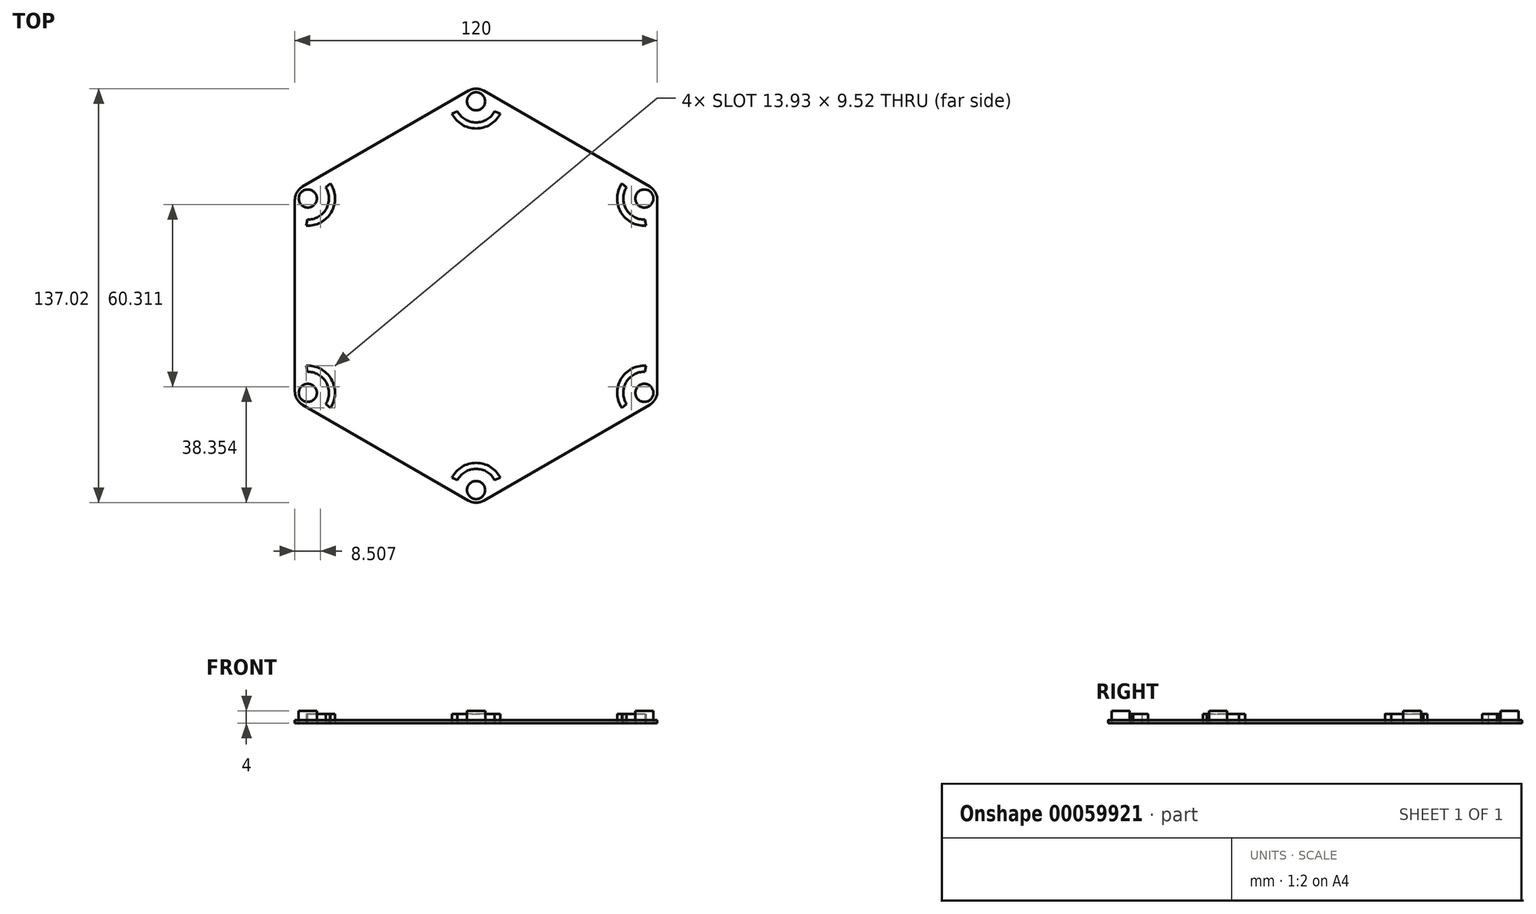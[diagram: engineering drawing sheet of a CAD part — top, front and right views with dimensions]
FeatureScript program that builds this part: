
annotation { "Feature Type Name" : "Feature", "Feature Type Description" : "" }
export const myFeature = defineFeature(function(context is Context, id is Id, definition is map)
    precondition{}
    {
        {
            var Q0;
            Q0=qCreatedBy(makeId("Top.planeOp"),FACE);
            var sketch = newSketch(context, id + "F0", { "sketchPlane" : qUnion([Q0])});
            skCircle(sketch, "E0.cCircle", {"center": v(0, 0) * mm, "radius": 60 * mm, "construction": true});
            skLineSegment(sketch, "E0.0", {"start": v(60, 31.75) * mm, "end": v(60, -31.75) * mm});
            skLineSegment(sketch, "E0.1", {"start": v(57.5, -36.08) * mm, "end": v(2.5, -67.84) * mm});
            skLineSegment(sketch, "E0.2", {"start": v(-2.5, -67.84) * mm, "end": v(-57.5, -36.08) * mm});
            skLineSegment(sketch, "E0.3", {"start": v(-60, -31.75) * mm, "end": v(-60, 31.75) * mm});
            skLineSegment(sketch, "E0.4", {"start": v(-57.5, 36.08) * mm, "end": v(-2.5, 67.84) * mm});
            skLineSegment(sketch, "E0.5", {"start": v(2.5, 67.84) * mm, "end": v(57.5, 36.08) * mm});
            skPoint(sketch, "E0.0.midPoint", {"position": v(60, 0) * mm});
            skCircle(sketch, "E1", {"center": v(0, -64.35) * mm, "radius": 3 * mm});
            skPoint(sketch, "E2.visualSharp", {"position": v(0, -69.28) * mm});
            skArc(sketch, "E2.filletArc", {"start": v(-2.5, -67.84) * mm, "mid": v(0, -68.5) * mm, "end": v(2.5, -67.84) * mm});
            skPoint(sketch, "E3.visualSharp", {"position": v(60, -34.64) * mm});
            skArc(sketch, "E3.filletArc", {"start": v(57.5, -36.08) * mm, "mid": v(59.33, -34.25) * mm, "end": v(60, -31.75) * mm});
            skPoint(sketch, "E4.visualSharp", {"position": v(-60, -34.64) * mm});
            skArc(sketch, "E4.filletArc", {"start": v(-60, -31.75) * mm, "mid": v(-59.33, -34.25) * mm, "end": v(-57.5, -36.08) * mm});
            skPoint(sketch, "E5.visualSharp", {"position": v(60, 34.64) * mm});
            skArc(sketch, "E5.filletArc", {"start": v(60, 31.75) * mm, "mid": v(59.33, 34.25) * mm, "end": v(57.5, 36.08) * mm});
            skPoint(sketch, "E6.visualSharp", {"position": v(-60, 34.64) * mm});
            skArc(sketch, "E6.filletArc", {"start": v(-57.5, 36.08) * mm, "mid": v(-59.33, 34.25) * mm, "end": v(-60, 31.75) * mm});
            skPoint(sketch, "E7.visualSharp", {"position": v(0, 69.28) * mm});
            skArc(sketch, "E7.filletArc", {"start": v(2.5, 67.84) * mm, "mid": v(0, 68.5) * mm, "end": v(-2.5, 67.84) * mm});
            skArc(sketch, "E8.0", {"start": v(6.15, -61.01) * mm, "mid": v(0, -57.35) * mm, "end": v(-6.15, -61.01) * mm});
            skArc(sketch, "E9.0", {"start": v(8.04, -60.31) * mm, "mid": v(0, -55.35) * mm, "end": v(-8.04, -60.31) * mm});
            skLineSegment(sketch, "E10.0", {"start": v(6.15, -61.01) * mm, "end": v(8.04, -60.31) * mm});
            skLineSegment(sketch, "E11.MirrorCS", {"start": v(-6.15, -61.01) * mm, "end": v(-8.04, -60.31) * mm});
            skCircle(sketch, "E12.1.0", {"center": v(-55.73, -32.18) * mm, "radius": 3 * mm});
            skArc(sketch, "E12.1.1", {"start": v(-49.76, -35.83) * mm, "mid": v(-49.67, -28.68) * mm, "end": v(-55.91, -25.18) * mm});
            skArc(sketch, "E12.1.2", {"start": v(-48.2, -37.12) * mm, "mid": v(-47.94, -27.68) * mm, "end": v(-56.25, -23.2) * mm});
            skLineSegment(sketch, "E12.1.3", {"start": v(-49.76, -35.83) * mm, "end": v(-48.2, -37.12) * mm});
            skLineSegment(sketch, "E12.1.4", {"start": v(-55.91, -25.18) * mm, "end": v(-56.25, -23.2) * mm});
            skCircle(sketch, "E12.2.0", {"center": v(-55.73, 32.18) * mm, "radius": 3 * mm});
            skArc(sketch, "E12.2.1", {"start": v(-55.91, 25.18) * mm, "mid": v(-49.67, 28.68) * mm, "end": v(-49.76, 35.83) * mm});
            skArc(sketch, "E12.2.2", {"start": v(-56.25, 23.2) * mm, "mid": v(-47.94, 27.68) * mm, "end": v(-48.2, 37.12) * mm});
            skLineSegment(sketch, "E12.2.3", {"start": v(-55.91, 25.18) * mm, "end": v(-56.25, 23.2) * mm});
            skLineSegment(sketch, "E12.2.4", {"start": v(-49.76, 35.83) * mm, "end": v(-48.2, 37.12) * mm});
            skCircle(sketch, "E12.3.0", {"center": v(0, 64.35) * mm, "radius": 3 * mm});
            skArc(sketch, "E12.3.1", {"start": v(-6.15, 61.01) * mm, "mid": v(0, 57.35) * mm, "end": v(6.15, 61.01) * mm});
            skArc(sketch, "E12.3.2", {"start": v(-8.04, 60.31) * mm, "mid": v(0, 55.35) * mm, "end": v(8.04, 60.31) * mm});
            skLineSegment(sketch, "E12.3.3", {"start": v(-6.15, 61.01) * mm, "end": v(-8.04, 60.31) * mm});
            skLineSegment(sketch, "E12.3.4", {"start": v(6.15, 61.01) * mm, "end": v(8.04, 60.31) * mm});
            skCircle(sketch, "E12.4.0", {"center": v(55.73, 32.18) * mm, "radius": 3 * mm});
            skArc(sketch, "E12.4.1", {"start": v(49.76, 35.83) * mm, "mid": v(49.67, 28.68) * mm, "end": v(55.91, 25.18) * mm});
            skArc(sketch, "E12.4.2", {"start": v(48.2, 37.12) * mm, "mid": v(47.94, 27.68) * mm, "end": v(56.25, 23.2) * mm});
            skLineSegment(sketch, "E12.4.3", {"start": v(49.76, 35.83) * mm, "end": v(48.2, 37.12) * mm});
            skLineSegment(sketch, "E12.4.4", {"start": v(55.91, 25.18) * mm, "end": v(56.25, 23.2) * mm});
            skCircle(sketch, "E12.5.0", {"center": v(55.73, -32.18) * mm, "radius": 3 * mm});
            skArc(sketch, "E12.5.1", {"start": v(55.91, -25.18) * mm, "mid": v(49.67, -28.68) * mm, "end": v(49.76, -35.83) * mm});
            skArc(sketch, "E12.5.2", {"start": v(56.25, -23.2) * mm, "mid": v(47.94, -27.68) * mm, "end": v(48.2, -37.12) * mm});
            skLineSegment(sketch, "E12.5.3", {"start": v(55.91, -25.18) * mm, "end": v(56.25, -23.2) * mm});
            skLineSegment(sketch, "E12.5.4", {"start": v(49.76, -35.83) * mm, "end": v(48.2, -37.12) * mm});
            skLineSegment(sketch, "E12.anchor1", {"start": v(0, 0) * mm, "end": v(0, -64.35) * mm, "construction": true});
            skLineSegment(sketch, "E12.anchor2", {"start": v(0, 0) * mm, "end": v(55.73, -32.18) * mm, "construction": true});
            skSolve(sketch);
        }
        {
            var Q0;
            Q0 = qSketchRegion(id + "F0", true);
            extrude(context, id + "F1", {"entities" : qUnion([Q0]), "depth" : 1 * mm});
        }
        {
            var Q0;
            Q0=makeQuery(id+"F0.imprint","IMPRINT",FACE,{"disambiguationData":[TD([[makeQuery(id+"F0.imprint","IMPRINT",EDGE,{"derivedFrom":sQuery(id+"F0.wireOp",EDGE,"E8.0")}),-1.0]])]});
            var Q1;
            Q1=makeQuery(id+"F0.imprint","IMPRINT",FACE,{"disambiguationData":[TD([[makeQuery(id+"F0.imprint","IMPRINT",EDGE,{"derivedFrom":sQuery(id+"F0.wireOp",EDGE,"E12.1.1")}),-1.0]])]});
            var Q2;
            Q2=makeQuery(id+"F0.imprint","IMPRINT",FACE,{"disambiguationData":[TD([[makeQuery(id+"F0.imprint","IMPRINT",EDGE,{"derivedFrom":sQuery(id+"F0.wireOp",EDGE,"E12.5.1")}),-1.0]])]});
            var Q3;
            Q3=makeQuery(id+"F0.imprint","IMPRINT",FACE,{"disambiguationData":[TD([[makeQuery(id+"F0.imprint","IMPRINT",EDGE,{"derivedFrom":sQuery(id+"F0.wireOp",EDGE,"E12.2.1")}),-1.0]])]});
            var Q4;
            Q4=makeQuery(id+"F0.imprint","IMPRINT",FACE,{"disambiguationData":[TD([[makeQuery(id+"F0.imprint","IMPRINT",EDGE,{"derivedFrom":sQuery(id+"F0.wireOp",EDGE,"E12.3.1")}),-1.0]])]});
            var Q5;
            Q5=makeQuery(id+"F0.imprint","IMPRINT",FACE,{"disambiguationData":[TD([[makeQuery(id+"F0.imprint","IMPRINT",EDGE,{"derivedFrom":sQuery(id+"F0.wireOp",EDGE,"E12.4.1")}),-1.0]])]});
            extrude(context, id + "F2", {"entities" : qUnion([Q0, Q1, Q2, Q3, Q4, Q5]), "depth" : 3 * mm});
        }
        {
            var Q0;
            Q0=makeQuery(id+"F0.imprint","IMPRINT",FACE,{"disambiguationData":[TD([[makeQuery(id+"F0.imprint","IMPRINT",EDGE,{"derivedFrom":sQuery(id+"F0.wireOp",EDGE,"E12.1.0")}),1.0]])]});
            var Q1;
            Q1=makeQuery(id+"F0.imprint","IMPRINT",FACE,{"disambiguationData":[TD([[makeQuery(id+"F0.imprint","IMPRINT",EDGE,{"derivedFrom":sQuery(id+"F0.wireOp",EDGE,"E1")}),1.0]])]});
            var Q2;
            Q2=makeQuery(id+"F0.imprint","IMPRINT",FACE,{"disambiguationData":[TD([[makeQuery(id+"F0.imprint","IMPRINT",EDGE,{"derivedFrom":sQuery(id+"F0.wireOp",EDGE,"E12.5.0")}),1.0]])]});
            var Q3;
            Q3=makeQuery(id+"F0.imprint","IMPRINT",FACE,{"disambiguationData":[TD([[makeQuery(id+"F0.imprint","IMPRINT",EDGE,{"derivedFrom":sQuery(id+"F0.wireOp",EDGE,"E12.4.0")}),1.0]])]});
            var Q4;
            Q4=makeQuery(id+"F0.imprint","IMPRINT",FACE,{"disambiguationData":[TD([[makeQuery(id+"F0.imprint","IMPRINT",EDGE,{"derivedFrom":sQuery(id+"F0.wireOp",EDGE,"E12.3.0")}),1.0]])]});
            var Q5;
            Q5=makeQuery(id+"F0.imprint","IMPRINT",FACE,{"disambiguationData":[TD([[makeQuery(id+"F0.imprint","IMPRINT",EDGE,{"derivedFrom":sQuery(id+"F0.wireOp",EDGE,"E12.2.0")}),1.0]])]});
            extrude(context, id + "F3", {"entities" : qUnion([Q0, Q1, Q2, Q3, Q4, Q5]), "depth" : 4 * mm});
        }
    });
